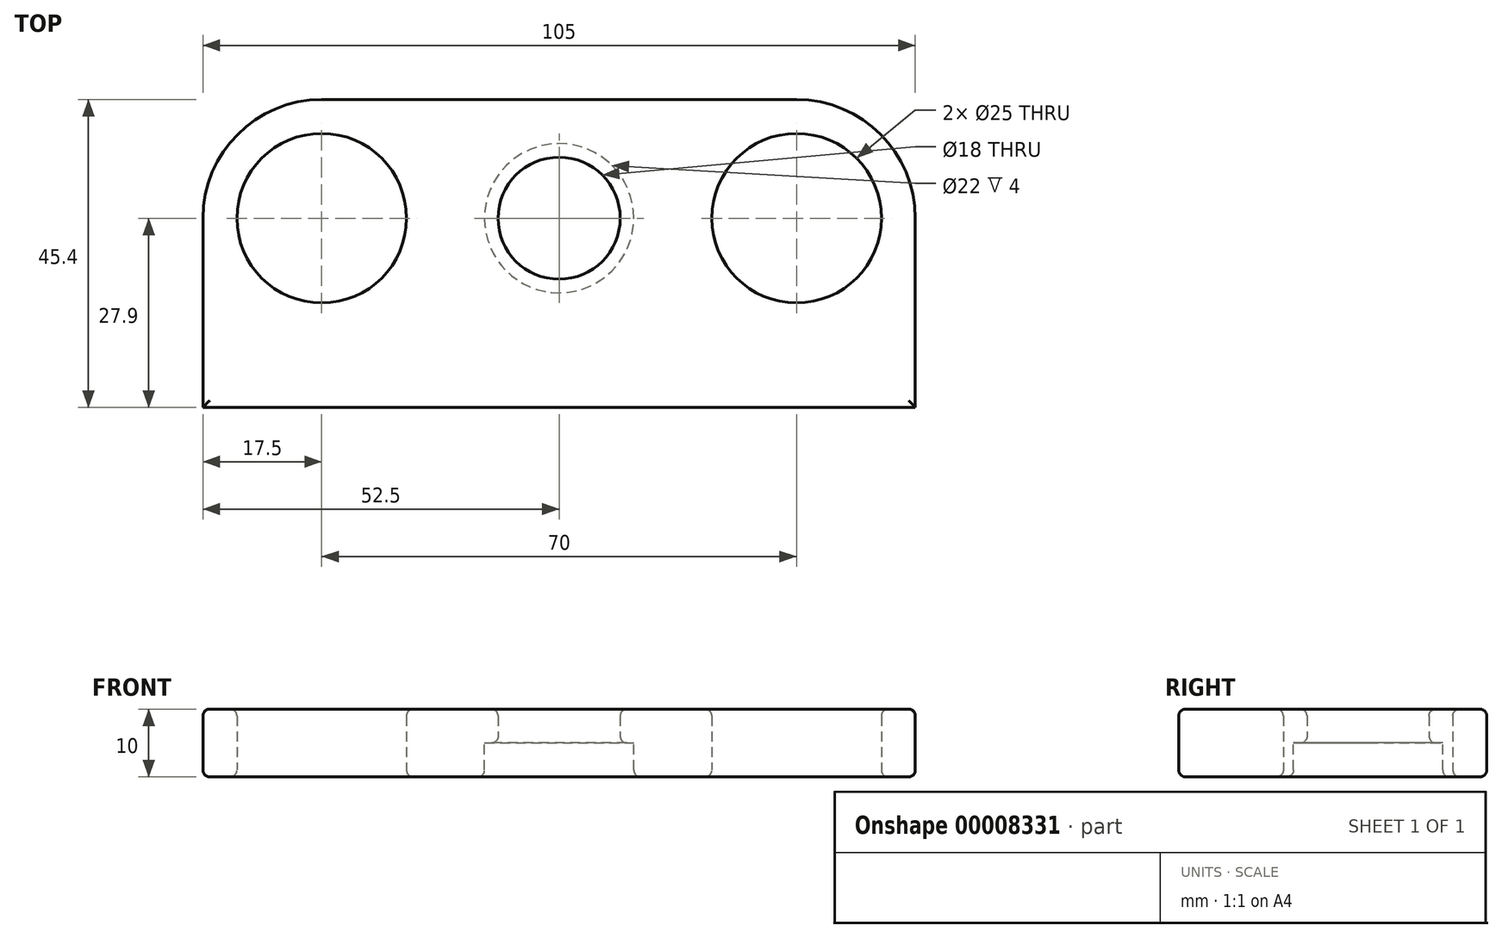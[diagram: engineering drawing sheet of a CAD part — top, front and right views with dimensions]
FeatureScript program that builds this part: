
annotation { "Feature Type Name" : "Feature", "Feature Type Description" : "" }
export const myFeature = defineFeature(function(context is Context, id is Id, definition is map)
    precondition{}
    {
        {
            var Q0;
            Q0=qCreatedBy(makeId("Top.planeOp"),FACE);
            var sketch = newSketch(context, id + "F0", { "sketchPlane" : qUnion([Q0])});
            skCircle(sketch, "E0", {"center": v(-35, 0) * mm, "radius": 12.5 * mm});
            skCircle(sketch, "E1", {"center": v(35, 0) * mm, "radius": 12.5 * mm});
            skLineSegment(sketch, "E2", {"start": v(-35, 17.5) * mm, "end": v(-21.68, 17.5) * mm});
            skArc(sketch, "E3", {"start": v(52.5, 0) * mm, "mid": v(47.37, 12.37) * mm, "end": v(35, 17.5) * mm});
            skArc(sketch, "E4", {"start": v(-35, 17.5) * mm, "mid": v(-47.37, 12.37) * mm, "end": v(-52.5, 0) * mm});
            skLineSegment(sketch, "E5", {"start": v(-52.5, 0) * mm, "end": v(-52.5, -27.9) * mm});
            skLineSegment(sketch, "E6", {"start": v(-52.5, -27.9) * mm, "end": v(52.5, -27.9) * mm});
            skLineSegment(sketch, "E7", {"start": v(52.5, -27.9) * mm, "end": v(52.5, 0) * mm});
            skLineSegment(sketch, "E8", {"start": v(21.68, 17.5) * mm, "end": v(35, 17.5) * mm});
            skCircle(sketch, "E9", {"center": v(0, 0) * mm, "radius": 9 * mm});
            skLineSegment(sketch, "E10", {"start": v(-21.68, 17.5) * mm, "end": v(21.68, 17.5) * mm});
            skSolve(sketch);
        }
        {
            var Q0;
            Q0=makeQuery(id+"F0.imprint","IMPRINT",FACE,{"disambiguationData":[TD([[makeQuery(id+"F0.imprint","IMPRINT",EDGE,{"derivedFrom":sQuery(id+"F0.wireOp",EDGE,"E0")}),-1.0]])]});
            extrude(context, id + "F1", {"entities" : qUnion([Q0]), "depth" : 5 * mm});
        }
        {
            var Q0;
            Q0=makeQuery(id+"F1.opExtrude","CAP_FACE",FACE,{"disambiguationData":[OSD([sQuery(id+"F0.wireOp",EDGE,"E0"),sQuery(id+"F0.wireOp",EDGE,"E1"),sQuery(id+"F0.wireOp",EDGE,"E2"),sQuery(id+"F0.wireOp",EDGE,"E3"),sQuery(id+"F0.wireOp",EDGE,"E4"),sQuery(id+"F0.wireOp",EDGE,"E5"),sQuery(id+"F0.wireOp",EDGE,"E6"),sQuery(id+"F0.wireOp",EDGE,"E7"),sQuery(id+"F0.wireOp",EDGE,"E8"),sQuery(id+"F0.wireOp",EDGE,"E9"),sQuery(id+"F0.wireOp",EDGE,"E10")])],"isStart":true});
            var sketch = newSketch(context, id + "F2", { "sketchPlane" : qUnion([Q0])});
            skCircle(sketch, "E11", {"center": v(0, 0) * mm, "radius": 11 * mm});
            skSolve(sketch);
        }
        {
            var Q0;
            Q0=makeQuery(id+"F2.imprint","IMPRINT",FACE,{"disambiguationData":[TD([[makeQuery(id+"F2.imprint","IMPRINT",EDGE,{"derivedFrom":sQuery(id+"F2.wireOp",EDGE,"E11")}),-1.0]])]});
            extrude(context, id + "F3", {"entities" : qUnion([Q0]), "operationType" : NewBodyOperationType.ADD, "depth" : 5 * mm});
        }
        {
            var Q0;
            Q0=makeQuery(id+"F1.opExtrude","CAP_EDGE",EDGE,{"disambiguationData":[OSD([sQuery(id+"F0.wireOp",EDGE,"E6")])],"isStart":false});
            var Q1;
            Q1=makeQuery(id+"F1.opExtrude","CAP_EDGE",EDGE,{"disambiguationData":[OSD([sQuery(id+"F0.wireOp",EDGE,"E9")])],"isStart":false});
            var Q2;
            Q2=makeQuery(id+"F1.opExtrude","CAP_EDGE",EDGE,{"disambiguationData":[OSD([sQuery(id+"F0.wireOp",EDGE,"E0")])],"isStart":false});
            var Q3;
            Q3=makeQuery(id+"F1.opExtrude","CAP_EDGE",EDGE,{"disambiguationData":[OSD([sQuery(id+"F0.wireOp",EDGE,"E1")])],"isStart":false});
            var Q4;
            Q4=makeQuery(id+"F1.opExtrude","CAP_EDGE",EDGE,{"disambiguationData":[OSD([sQuery(id+"F0.wireOp",EDGE,"E2"),sQuery(id+"F0.wireOp",EDGE,"E8"),sQuery(id+"F0.wireOp",EDGE,"E10")])],"isStart":false});
            var Q5;
            Q5=makeQuery(id+"F1.opExtrude","CAP_EDGE",EDGE,{"disambiguationData":[OSD([sQuery(id+"F0.wireOp",EDGE,"E5")])],"isStart":false});
            var Q6;
            Q6=makeQuery(id+"F3.opExtrude","CAP_EDGE",EDGE,{"disambiguationData":[OSD([sQuery(id+"F0.wireOp",EDGE,"E6")])],"isStart":false});
            var Q7;
            Q7=makeQuery(id+"F3.opExtrude","CAP_EDGE",EDGE,{"disambiguationData":[OSD([sQuery(id+"F0.wireOp",EDGE,"E7")])],"isStart":false});
            var Q8;
            Q8=makeQuery(id+"F3.opExtrude","CAP_EDGE",EDGE,{"disambiguationData":[OSD([sQuery(id+"F0.wireOp",EDGE,"E1")])],"isStart":false});
            var Q9;
            Q9=makeQuery(id+"F3.opExtrude","CAP_EDGE",EDGE,{"disambiguationData":[OSD([sQuery(id+"F2.wireOp",EDGE,"E11")])],"isStart":false});
            var Q10;
            Q10=makeQuery(id+"F1.opExtrude","CAP_EDGE",EDGE,{"disambiguationData":[OSD([sQuery(id+"F0.wireOp",EDGE,"E9")])],"isStart":true});
            var Q11;
            Q11=makeQuery(id+"F3.opExtrude","CAP_EDGE",EDGE,{"disambiguationData":[OSD([sQuery(id+"F0.wireOp",EDGE,"E0")])],"isStart":false});
            fillet(context, id + "F4", {"entities" : qUnion([Q0, Q1, Q2, Q3, Q4, Q5, Q6, Q7, Q8, Q9, Q10, Q11]), "radius" : 1 * mm, "tangentPropagation" : true, "allowEdgeOverflow" : false});
        }
    });
